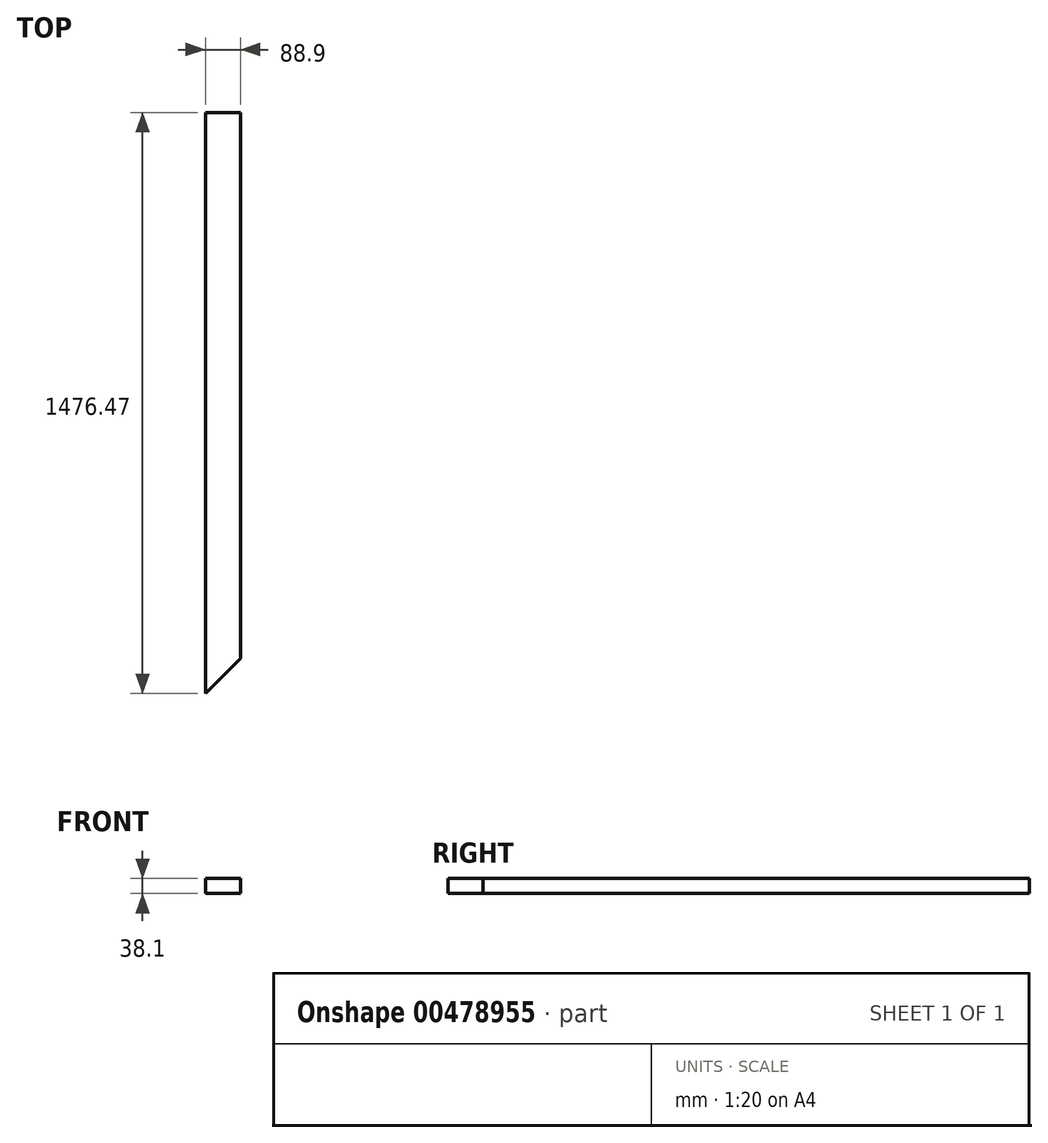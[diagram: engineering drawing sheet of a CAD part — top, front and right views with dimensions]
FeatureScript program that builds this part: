
annotation { "Feature Type Name" : "Feature", "Feature Type Description" : "" }
export const myFeature = defineFeature(function(context is Context, id is Id, definition is map)
    precondition{}
    {
        {
            var Q0;
            Q0=qCreatedBy(makeId("Front.planeOp"),FACE);
            var sketch = newSketch(context, id + "F0", { "sketchPlane" : qUnion([Q0])});
            skLineSegment(sketch, "E0.bottom", {"start": v(0, 0) * mm, "end": v(88.9, 0) * mm});
            skLineSegment(sketch, "E0.top", {"start": v(0, 38.1) * mm, "end": v(88.9, 38.1) * mm});
            skLineSegment(sketch, "E0.left", {"start": v(0, 0) * mm, "end": v(0, 38.1) * mm});
            skLineSegment(sketch, "E0.right", {"start": v(88.9, 0) * mm, "end": v(88.9, 38.1) * mm});
            skSolve(sketch);
        }
        {
            var Q0;
            Q0 = qSketchRegion(id + "F0", true);
            extrude(context, id + "F1", {"entities" : qUnion([Q0]), "depth" : 1476.47 * mm});
        }
        {
            var Q0;
            Q0=makeQuery(id+"F1.opExtrude","SWEPT_FACE",FACE,{"disambiguationData":[OSD([sQuery(id+"F0.wireOp",EDGE,"E0.top")])]});
            var sketch = newSketch(context, id + "F2", { "sketchPlane" : qUnion([Q0])});
            skLineSegment(sketch, "E1", {"start": v(0, -1476.47) * mm, "end": v(88.9, -1387.57) * mm});
            skLineSegment(sketch, "E2", {"start": v(88.9, -1387.57) * mm, "end": v(88.9, -1476.47) * mm});
            skLineSegment(sketch, "E3", {"start": v(88.9, -1476.47) * mm, "end": v(0, -1476.47) * mm});
            skSolve(sketch);
        }
        {
            var Q0;
            Q0 = qSketchRegion(id + "F2", true);
            extrude(context, id + "F3", {"entities" : qUnion([Q0]), "operationType" : NewBodyOperationType.REMOVE, "oppositeDirection" : true, "depth" : 104.14 * mm});
        }
    });
